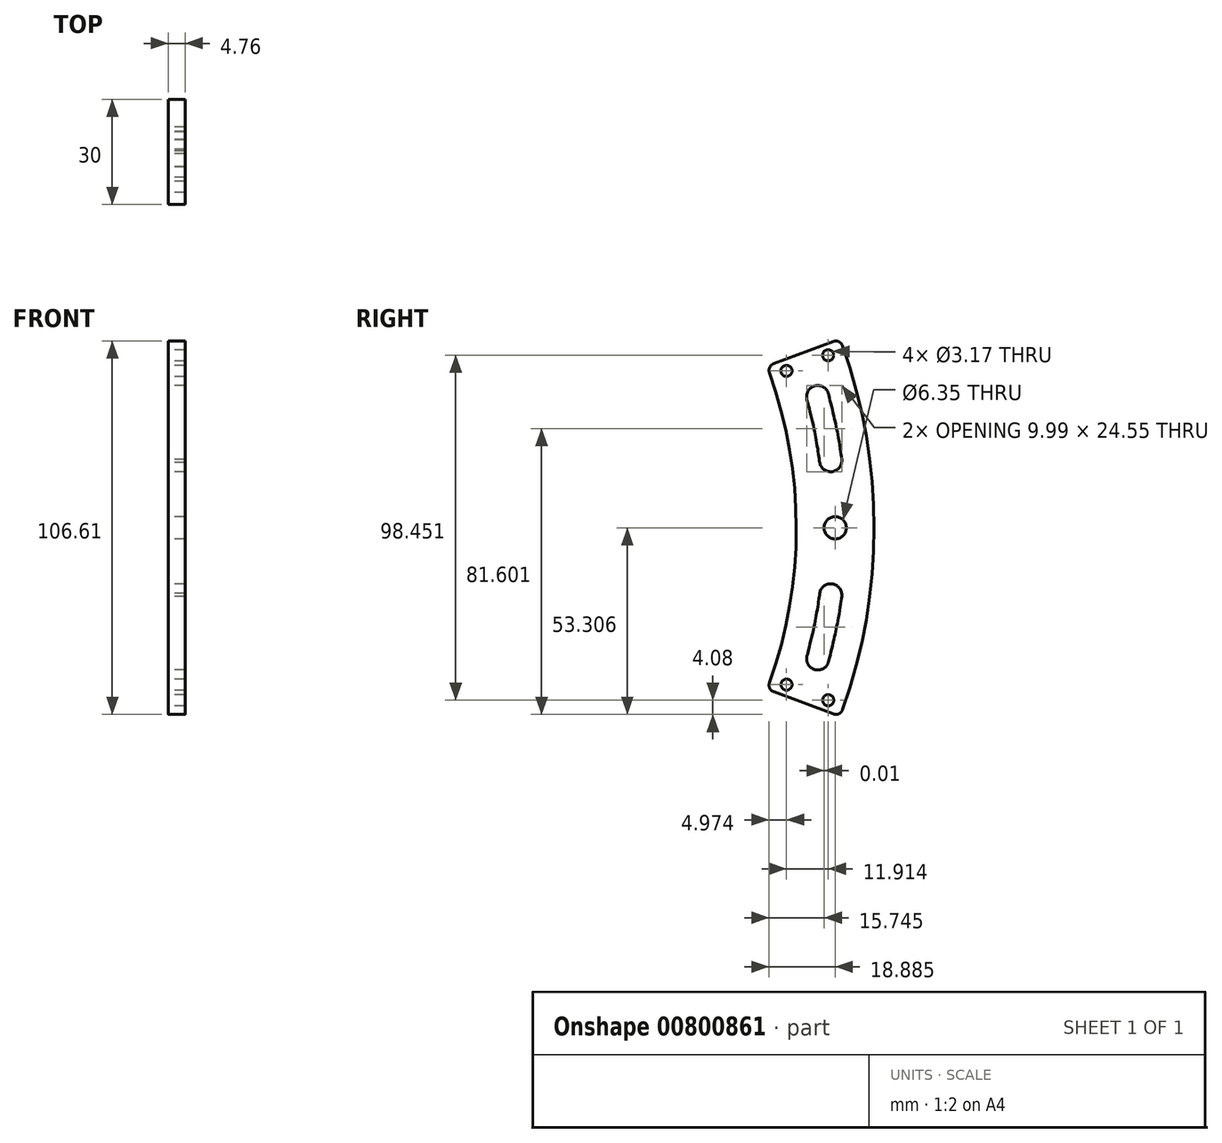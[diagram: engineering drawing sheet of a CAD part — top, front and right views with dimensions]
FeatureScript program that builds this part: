
annotation { "Feature Type Name" : "Feature", "Feature Type Description" : "" }
export const myFeature = defineFeature(function(context is Context, id is Id, definition is map)
    precondition{}
    {
        {
            var Q0;
            Q0=qCreatedBy(makeId("Right.planeOp"),FACE);
            var sketch = newSketch(context, id + "F0", { "sketchPlane" : qUnion([Q0])});
            skLineSegment(sketch, "E0", {"start": v(0, 0) * mm, "end": v(142.87, 0.03) * mm, "construction": true});
            skArc(sketch, "E1", {"start": v(124.1, 44.27) * mm, "mid": v(131.76, -0.96) * mm, "end": v(123.44, -46.08) * mm});
            skArc(sketch, "E2", {"start": v(144.96, -51.95) * mm, "mid": v(153.99, 0.03) * mm, "end": v(144.94, 52) * mm});
            skLineSegment(sketch, "E3", {"start": v(142.36, 53.2) * mm, "end": v(125.29, 46.82) * mm});
            skPoint(sketch, "E4.orphan", {"position": v(0, 131.76) * mm});
            skPoint(sketch, "E5.orphan", {"position": v(0, 142.88) * mm});
            skPoint(sketch, "E6.orphan", {"position": v(0, 153.99) * mm});
            skLineSegment(sketch, "E7.MirrorCS", {"start": v(142.38, -53.15) * mm, "end": v(125.3, -46.77) * mm});
            skLineSegment(sketch, "E8.MirrorCS", {"start": v(146.36, -47.86) * mm, "end": v(145.74, -47.63) * mm});
            skPoint(sketch, "E9.orphan", {"position": v(0, -131.76) * mm});
            skPoint(sketch, "E10.orphan", {"position": v(0, -142.88) * mm});
            skPoint(sketch, "E11.orphan", {"position": v(0, -147.64) * mm});
            skPoint(sketch, "E12.orphan", {"position": v(0, -153.99) * mm});
            skPoint(sketch, "E13.trimOffspring.end.orphan", {"position": v(125.66, -40.14) * mm});
            skPoint(sketch, "E14.orphan", {"position": v(125.64, 40.18) * mm});
            skArc(sketch, "E15", {"start": v(131.2, -12.2) * mm, "mid": v(128.66, -28.43) * mm, "end": v(124.12, -44.23) * mm, "construction": true});
            skArc(sketch, "E16.trimOffspring", {"start": v(123.44, -46.08) * mm, "mid": v(120.46, -53.4) * mm, "end": v(117.04, -60.53) * mm, "construction": true});
            skPoint(sketch, "E17.visualSharp", {"position": v(124.88, -42.02) * mm});
            skPoint(sketch, "E18.visualSharp", {"position": v(129.06, -48.18) * mm});
            skLineSegment(sketch, "E19", {"start": v(134.37, 47.05) * mm, "end": v(134.98, 46.84) * mm, "construction": true});
            skPoint(sketch, "E20.orphan", {"position": v(148.05, 42.35) * mm});
            skLineSegment(sketch, "E21", {"start": v(134.98, 46.84) * mm, "end": v(134.44, 46.66) * mm, "construction": true});
            skLineSegment(sketch, "E22", {"start": v(128.96, 44.8) * mm, "end": v(130.45, 45.36) * mm, "construction": true});
            skCircle(sketch, "E23", {"center": v(128.96, 44.8) * mm, "radius": 1.59 * mm});
            skCircle(sketch, "E24", {"center": v(140.86, 49.25) * mm, "radius": 1.59 * mm});
            skCircle(sketch, "E25.MirrorC", {"center": v(128.98, -44.76) * mm, "radius": 1.59 * mm});
            skCircle(sketch, "E26.MirrorC", {"center": v(140.88, -49.2) * mm, "radius": 1.59 * mm});
            skLineSegment(sketch, "E27.0", {"start": v(141.15, -6.32) * mm, "end": v(142.88, -6.32) * mm, "construction": true});
            skCircle(sketch, "E28", {"center": v(142.87, 0.03) * mm, "radius": 3.18 * mm});
            skPoint(sketch, "E29.startSnap0", {"position": v(138.35, 25.02) * mm});
            skLineSegment(sketch, "E30", {"start": v(141.59, 19.13) * mm, "end": v(141.49, 19.1) * mm});
            skArc(sketch, "E31.trimOffspring", {"start": v(141.77, -2.95) * mm, "mid": v(141.47, -4.64) * mm, "end": v(141.15, -6.32) * mm, "construction": true});
            skLineSegment(sketch, "E32.trimOffspring", {"start": v(137.78, 37.42) * mm, "end": v(137.88, 37.45) * mm});
            skFitSpline(sketch, "E33.0", {"points": [v(134.8, 36.7) * mm, v(135.2, 35.03) * mm, v(136.02, 31.74) * mm, v(136.91, 27.83) * mm, v(137.47, 24.94) * mm, v(137.94, 22.12) * mm, v(138.24, 20.06) * mm, v(138.45, 18.67) * mm]});
            skFitSpline(sketch, "E34.0", {"points": [v(140.96, 38.22) * mm, v(141.17, 37.39) * mm, v(141.58, 35.73) * mm, v(142.18, 33.24) * mm, v(142.66, 31.2) * mm, v(143.01, 29.59) * mm, v(143.35, 28) * mm, v(143.72, 26.06) * mm, v(144.22, 23.09) * mm, v(144.53, 20.98) * mm, v(144.73, 19.59) * mm]});
            skArc(sketch, "E35", {"start": v(134.8, 36.7) * mm, "mid": v(137.11, 40.54) * mm, "end": v(140.96, 38.22) * mm});
            skArc(sketch, "E36", {"start": v(138.45, 18.67) * mm, "mid": v(142.04, 16.05) * mm, "end": v(144.73, 19.59) * mm});
            skLineSegment(sketch, "E37.MirrorCS", {"start": v(136.4, -36.84) * mm, "end": v(136.65, -36.94) * mm});
            skLineSegment(sketch, "E38.MirrorCS", {"start": v(137.8, -37.37) * mm, "end": v(137.9, -37.4) * mm});
            skLineSegment(sketch, "E39.MirrorCS", {"start": v(141.6, -19.08) * mm, "end": v(141.5, -19.06) * mm});
            skLineSegment(sketch, "E40.MirrorCS", {"start": v(138.36, -26.77) * mm, "end": v(140.28, -27.12) * mm, "construction": true});
            skArc(sketch, "E41.MirrorCS", {"start": v(134.8, -36.64) * mm, "mid": v(137.13, -40.49) * mm, "end": v(140.97, -38.17) * mm});
            skFitSpline(sketch, "E42.MirrorCS", {"points": [v(134.8, -36.64) * mm, v(135.22, -34.98) * mm, v(136.04, -31.69) * mm, v(136.92, -27.78) * mm, v(137.48, -24.89) * mm, v(137.95, -22.07) * mm, v(138.25, -20.01) * mm, v(138.45, -18.62) * mm]});
            skPoint(sketch, "E43.MirrorP", {"position": v(138.36, -24.97) * mm});
            skPoint(sketch, "E44.MirrorP", {"position": v(148.07, -42.3) * mm});
            skArc(sketch, "E45.MirrorCS", {"start": v(138.45, -18.62) * mm, "mid": v(142.04, -16) * mm, "end": v(144.74, -19.53) * mm});
            skFitSpline(sketch, "E46.0", {"points": [v(140.97, -38.17) * mm, v(141.18, -37.34) * mm, v(141.6, -35.68) * mm, v(142.2, -33.2) * mm, v(142.67, -31.15) * mm, v(143.02, -29.54) * mm, v(143.36, -27.94) * mm, v(143.73, -26) * mm, v(144.23, -23.04) * mm, v(144.54, -20.93) * mm, v(144.74, -19.53) * mm]});
            skPoint(sketch, "E47.visualSharp", {"position": v(123.43, 46.12) * mm});
            skArc(sketch, "E47.filletArc", {"start": v(125.29, 46.82) * mm, "mid": v(124.17, 45.79) * mm, "end": v(124.1, 44.27) * mm});
            skPoint(sketch, "E48.visualSharp", {"position": v(144.24, 53.9) * mm});
            skArc(sketch, "E48.filletArc", {"start": v(144.94, 52) * mm, "mid": v(143.9, 53.14) * mm, "end": v(142.36, 53.2) * mm});
            skLineSegment(sketch, "E49.trimOffspring", {"start": v(124.5, 43.14) * mm, "end": v(123.8, 42.87) * mm, "construction": true});
            skLineSegment(sketch, "E50.trimOffspring", {"start": v(134.69, 46.94) * mm, "end": v(134.4, 46.84) * mm, "construction": true});
            skPoint(sketch, "E51.orphan", {"position": v(133.83, 50.01) * mm});
            skLineSegment(sketch, "E52.trimOffspring", {"start": v(134.4, 46.84) * mm, "end": v(134.69, 46.94) * mm, "construction": true});
            skLineSegment(sketch, "E53.trimOffspring", {"start": v(134.44, 46.66) * mm, "end": v(134.37, 47.05) * mm, "construction": true});
            skPoint(sketch, "E54.0.start.orphan", {"position": v(145.73, 47.68) * mm});
            skPoint(sketch, "E55.end.orphan", {"position": v(136.64, 36.99) * mm});
            skPoint(sketch, "E55.start.orphan", {"position": v(136.39, 36.9) * mm});
            skPoint(sketch, "E29.end.orphan", {"position": v(140.27, 27.17) * mm});
            skPoint(sketch, "E29.start.orphan", {"position": v(138.35, 26.82) * mm});
            skArc(sketch, "E56.trimOffspring", {"start": v(136.4, -36.84) * mm, "mid": v(136.02, -38.23) * mm, "end": v(135.62, -39.62) * mm, "construction": true});
            skPoint(sketch, "E57.visualSharp", {"position": v(123.44, -46.08) * mm});
            skArc(sketch, "E57.filletArc", {"start": v(124.12, -44.23) * mm, "mid": v(124.19, -45.75) * mm, "end": v(125.3, -46.77) * mm});
            skPoint(sketch, "E58.visualSharp", {"position": v(144.26, -53.85) * mm});
            skArc(sketch, "E58.filletArc", {"start": v(142.38, -53.15) * mm, "mid": v(143.92, -53.09) * mm, "end": v(144.96, -51.95) * mm});
            skSolve(sketch);
        }
        {
            var Q0;
            Q0=qSketchRegion(id+"F0",true);
            extrude(context, id + "F1", {"entities" : qUnion([Q0]), "depth" : 4.76 * mm, "offsetDistance" : 25 * mm});
        }
    });
